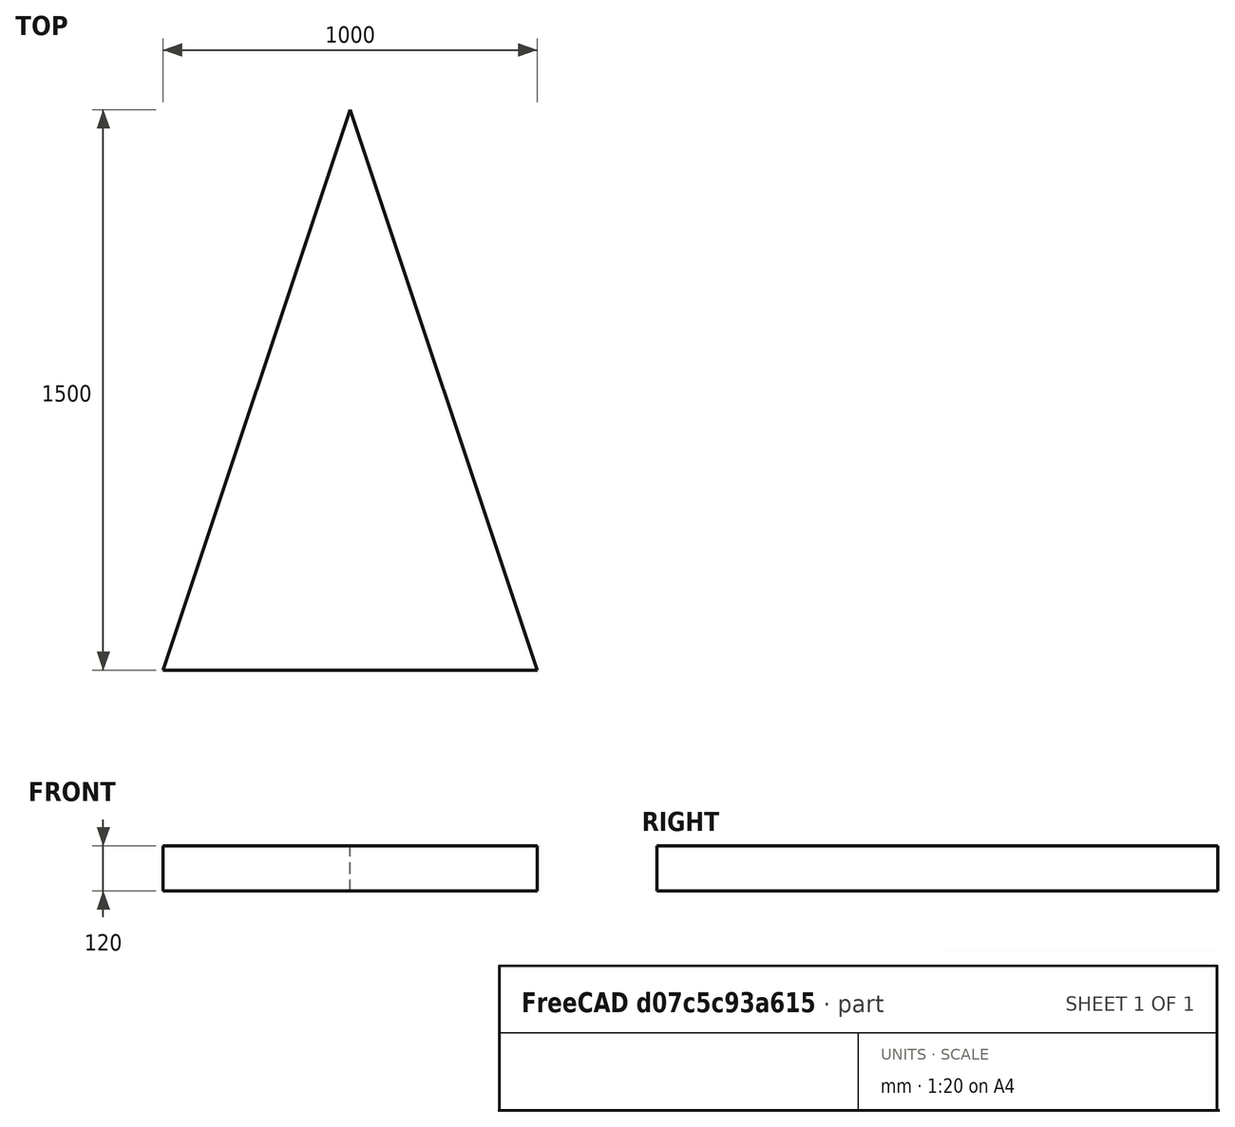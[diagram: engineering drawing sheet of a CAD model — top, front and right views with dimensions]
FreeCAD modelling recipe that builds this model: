
FCSTD DOCUMENT  (FreeCAD 0.18.4R)
Label: Placa
License: All rights reserved
LicenseURL: http://en.wikipedia.org/wiki/All_rights_reserved
objects: Sketcher::SketchObject×1, PartDesign::Pad×1, PartDesign::Body×1
note: 4 computed .brp shape members not serialized (recipe doc carries the construction recipe); baked Part::Feature solids carry a one-line shape summary decoded from their .brp

FEATURE [Sketcher::SketchObject] Sketch
  MapMode = 5
  Support = -> [XY_Plane]
  sketch-geometry (4):
    g0: LineSegment StartX=0 StartY=0 StartZ=0 EndX=500 EndY=0 EndZ=0
    g1: LineSegment StartX=500 StartY=0 StartZ=0 EndX=-5.68e-14 EndY=1500 EndZ=0
    g2: LineSegment StartX=-5.68e-14 StartY=1500 StartZ=0 EndX=-500 EndY=0 EndZ=0
    g3: LineSegment StartX=-500 StartY=0 StartZ=0 EndX=0 EndY=0 EndZ=0
  constraints (11):
    c: Coincident(g-1,g0)
    c: PointOnObject(g0,g-1)
    c: Coincident(g0,g1)
    c: PointOnObject(g1,g-2)
    c: Coincident(g1,g2)
    c: PointOnObject(g2,g-1)
    c: Coincident(g2,g3)
    c: Coincident(g3,g0)
    c: DistanceX(g2,g0) = 500
    c: DistanceX(g0,g0) = 500
    c: DistanceY(g0,g1) = 1500
FEATURE [PartDesign::Pad] Pad
  Length = 120
  Length2 = 100
  Profile = -> Sketch
  Type = 0
FEATURE [PartDesign::Body] Body
  Group = -> [Sketch,Pad]
  Origin = -> Origin
  Tip = -> Pad
